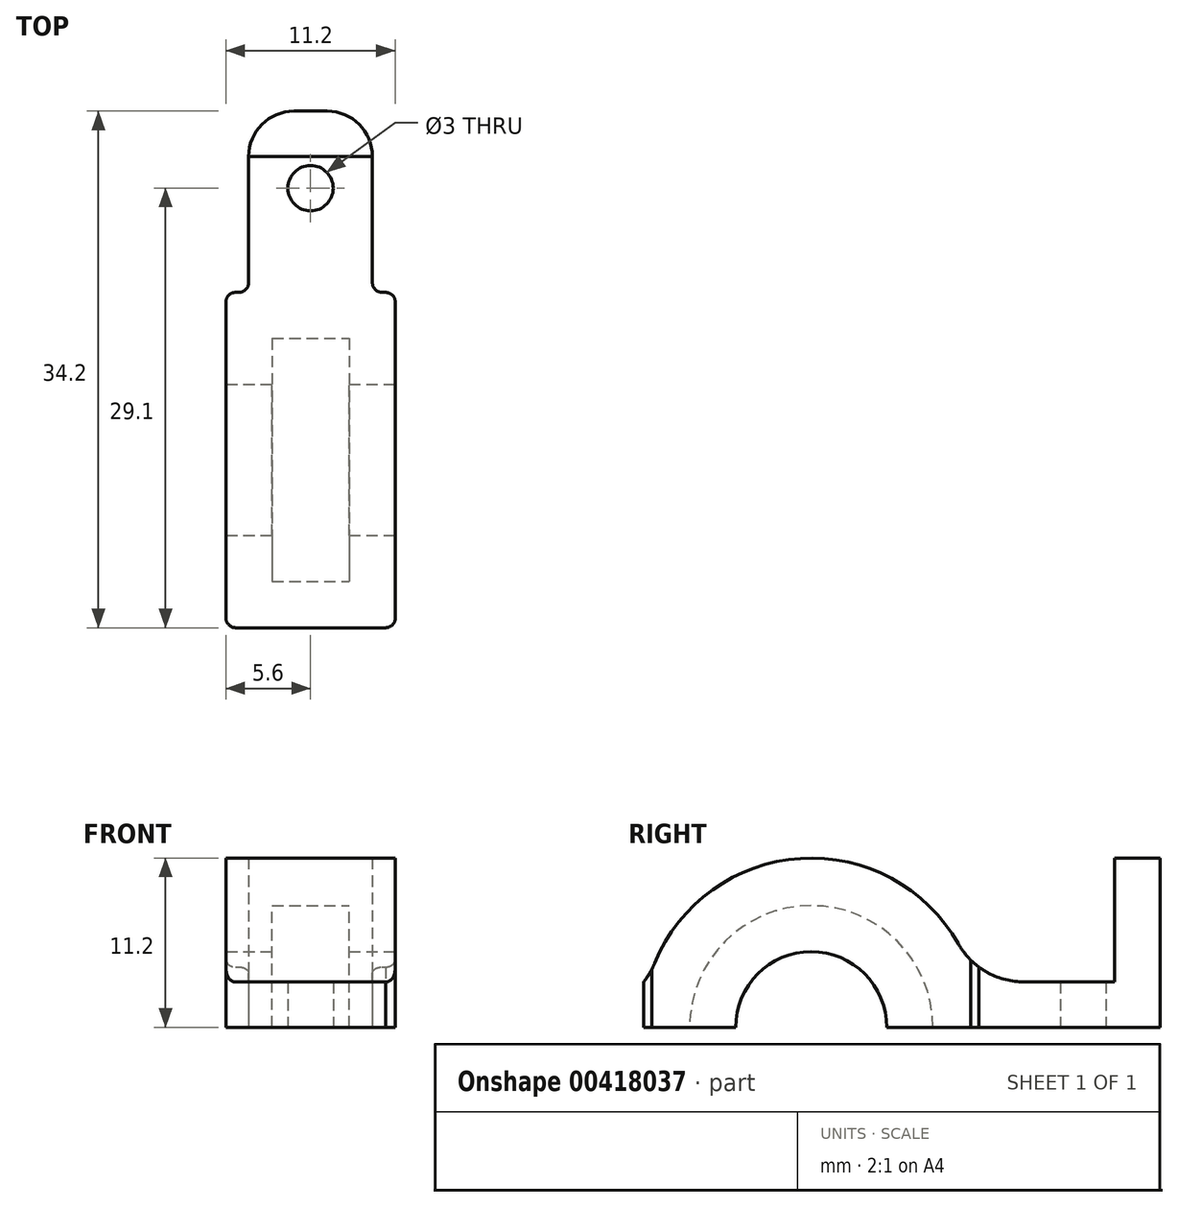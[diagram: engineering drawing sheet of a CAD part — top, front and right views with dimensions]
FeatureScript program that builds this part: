
annotation { "Feature Type Name" : "Feature", "Feature Type Description" : "" }
export const myFeature = defineFeature(function(context is Context, id is Id, definition is map)
    precondition{}
    {
        {
            var Q0;
            Q0=qCreatedBy(makeId("Top.planeOp"),FACE);
            var sketch = newSketch(context, id + "F0", { "sketchPlane" : qUnion([Q0])});
            skLineSegment(sketch, "E0", {"start": v(0, 0) * mm, "end": v(2.6, 0) * mm, "construction": true});
            skLineSegment(sketch, "E1", {"start": v(2.6, 0) * mm, "end": v(2.6, 8.1) * mm});
            skLineSegment(sketch, "E2", {"start": v(2.6, 8.1) * mm, "end": v(2.6, -8.1) * mm});
            skLineSegment(sketch, "E3.MirrorCS", {"start": v(-2.6, 8.1) * mm, "end": v(-2.6, -8.1) * mm});
            skLineSegment(sketch, "E4", {"start": v(2.6, 8.1) * mm, "end": v(-2.6, 8.1) * mm});
            skLineSegment(sketch, "E5", {"start": v(-2.6, -8.1) * mm, "end": v(2.6, -8.1) * mm});
            skLineSegment(sketch, "E6.0", {"start": v(4.97, 11.1) * mm, "end": v(4.73, 11.1) * mm});
            skLineSegment(sketch, "E6.1", {"start": v(5.6, 10.57) * mm, "end": v(5.6, -11.1) * mm});
            skLineSegment(sketch, "E6.3", {"start": v(-5.6, 10.47) * mm, "end": v(-5.6, -11.1) * mm});
            skCircle(sketch, "E7", {"center": v(0, 18) * mm, "radius": 1.5 * mm});
            skLineSegment(sketch, "E8", {"start": v(-4.1, 11.73) * mm, "end": v(-4.1, 20.1) * mm});
            skLineSegment(sketch, "E9.MirrorCS", {"start": v(4.1, 11.73) * mm, "end": v(4.1, 20.1) * mm});
            skLineSegment(sketch, "E10", {"start": v(-1.1, 23.1) * mm, "end": v(1.1, 23.1) * mm});
            skLineSegment(sketch, "E11.trimOffspring", {"start": v(-4.73, 11.1) * mm, "end": v(-4.97, 11.1) * mm});
            skPoint(sketch, "E12.visualSharp", {"position": v(-4.1, 11.1) * mm});
            skArc(sketch, "E12.filletArc", {"start": v(-4.73, 11.1) * mm, "mid": v(-4.29, 11.29) * mm, "end": v(-4.1, 11.73) * mm});
            skPoint(sketch, "E13.visualSharp", {"position": v(-5.6, 11.1) * mm});
            skArc(sketch, "E13.filletArc", {"start": v(-4.97, 11.1) * mm, "mid": v(-5.41, 10.91) * mm, "end": v(-5.6, 10.47) * mm});
            skPoint(sketch, "E14.visualSharp", {"position": v(-4.1, 23.1) * mm});
            skArc(sketch, "E14.filletArc", {"start": v(-1.1, 23.1) * mm, "mid": v(-3.22, 22.22) * mm, "end": v(-4.1, 20.1) * mm});
            skArc(sketch, "E15.MirrorCS", {"start": v(1.1, 23.1) * mm, "mid": v(3.22, 22.22) * mm, "end": v(4.1, 20.1) * mm});
            skArc(sketch, "E16.MirrorCS", {"start": v(4.97, 11.1) * mm, "mid": v(5.38, 10.95) * mm, "end": v(5.6, 10.57) * mm});
            skArc(sketch, "E17.MirrorCS", {"start": v(4.73, 11.1) * mm, "mid": v(4.29, 11.29) * mm, "end": v(4.1, 11.73) * mm});
            skPoint(sketch, "E18.orphan", {"position": v(4.1, 11.1) * mm});
            skPoint(sketch, "E19.orphan", {"position": v(4.1, 23.1) * mm});
            skLineSegment(sketch, "E20", {"start": v(-4.73, 11.1) * mm, "end": v(4.73, 11.1) * mm});
            skArc(sketch, "E21.MirrorCS", {"start": v(-4.73, -11.1) * mm, "mid": v(-4.29, -11.29) * mm, "end": v(-4.1, -11.73) * mm});
            skLineSegment(sketch, "E22.MirrorCS", {"start": v(-4.73, -11.1) * mm, "end": v(-4.97, -11.1) * mm});
            skArc(sketch, "E23.MirrorCS", {"start": v(-4.97, -11.1) * mm, "mid": v(-5.41, -10.91) * mm, "end": v(-5.6, -10.47) * mm});
            skArc(sketch, "E24.MirrorCS", {"start": v(4.73, -11.1) * mm, "mid": v(4.29, -11.29) * mm, "end": v(4.1, -11.73) * mm});
            skLineSegment(sketch, "E25.MirrorCS", {"start": v(4.97, -11.1) * mm, "end": v(4.73, -11.1) * mm});
            skArc(sketch, "E26.MirrorCS", {"start": v(4.97, -11.1) * mm, "mid": v(5.38, -10.95) * mm, "end": v(5.6, -10.57) * mm});
            skPoint(sketch, "E27.MirrorP", {"position": v(-4.1, -11.1) * mm});
            skPoint(sketch, "E28.MirrorP", {"position": v(-5.6, -11.1) * mm});
            skLineSegment(sketch, "E29.MirrorCS", {"start": v(-4.73, -11.1) * mm, "end": v(4.73, -11.1) * mm});
            skPoint(sketch, "E30.MirrorP", {"position": v(4.1, -23.1) * mm});
            skArc(sketch, "E31.MirrorCS", {"start": v(1.1, -23.1) * mm, "mid": v(3.22, -22.22) * mm, "end": v(4.1, -20.1) * mm});
            skCircle(sketch, "E32.MirrorC", {"center": v(0, -18) * mm, "radius": 1.5 * mm});
            skLineSegment(sketch, "E33.MirrorCS", {"start": v(-4.1, -11.73) * mm, "end": v(-4.1, -20.1) * mm});
            skPoint(sketch, "E34.MirrorP", {"position": v(-4.1, -23.1) * mm});
            skPoint(sketch, "E35.MirrorP", {"position": v(4.1, -11.1) * mm});
            skLineSegment(sketch, "E36.MirrorCS", {"start": v(4.1, -11.73) * mm, "end": v(4.1, -20.1) * mm});
            skLineSegment(sketch, "E37.MirrorCS", {"start": v(-1.1, -23.1) * mm, "end": v(1.1, -23.1) * mm});
            skArc(sketch, "E38.MirrorCS", {"start": v(-1.1, -23.1) * mm, "mid": v(-3.22, -22.22) * mm, "end": v(-4.1, -20.1) * mm});
            skLineSegment(sketch, "E39", {"start": v(0, 0) * mm, "end": v(5.6, 0) * mm});
            skLineSegment(sketch, "E40", {"start": v(0, 0) * mm, "end": v(-2.6, 0) * mm});
            skLineSegment(sketch, "E41.bottom", {"start": v(-2.55, -8.05) * mm, "end": v(2.55, -8.05) * mm});
            skLineSegment(sketch, "E41.top", {"start": v(-2.55, 8.05) * mm, "end": v(2.55, 8.05) * mm});
            skLineSegment(sketch, "E41.left", {"start": v(-2.55, -8.05) * mm, "end": v(-2.55, 8.05) * mm});
            skLineSegment(sketch, "E41.right", {"start": v(2.55, -8.05) * mm, "end": v(2.55, 8.05) * mm});
            skPoint(sketch, "E41.middle", {"position": v(0, 0) * mm});
            skSolve(sketch);
        }
        {
            var Q0;
            Q0=makeQuery(id+"F0.imprint","IMPRINT",FACE,{"disambiguationData":[TD([[makeQuery(id+"F0.imprint","IMPRINT",EDGE,{"derivedFrom":sQuery(id+"F0.wireOp",EDGE,"E7")}),-1.0]])]});
            var Q1;
            Q1=makeQuery(id+"F0.imprint","IMPRINT",FACE,{"disambiguationData":[TD([[makeQuery(id+"F0.imprint","IMPRINT",EDGE,{"derivedFrom":sQuery(id+"F0.wireOp",EDGE,"E3.MirrorCS")}),-1.0]])]});
            var Q2;
            {var subQ1=sQuery(id+"F0.wireOp",EDGE,"7e61b978-d09d-4bad-839f-0245cd0e4011.MirrorCS");Q2=makeQuery(id+"F0.imprint","IMPRINT",FACE,{"disambiguationData":[TD([[makeQuery(id+"F0.imprint","IMPRINT",EDGE,{"derivedFrom":subQ1}),1.0]])]});}
            var Q3;
            Q3=makeQuery(id+"F0.imprint","IMPRINT",FACE,{"disambiguationData":[TD([[makeQuery(id+"F0.imprint","IMPRINT",EDGE,{"derivedFrom":sQuery(id+"F0.wireOp",EDGE,"E3.MirrorCS")}),1.0]])]});
            var Q4;
            Q4=makeQuery(id+"F0.imprint","IMPRINT",FACE,{"disambiguationData":[TD([[makeQuery(id+"F0.imprint","IMPRINT",EDGE,{"derivedFrom":sQuery(id+"F0.wireOp",EDGE,"E21.MirrorCS")}),1.0]])]});
            var Q5;
            {var subQ1=sQuery(id+"F0.wireOp",EDGE,"E41.bottom");Q5=makeQuery(id+"F0.imprint","IMPRINT",FACE,{"disambiguationData":[TD([[makeQuery(id+"F0.imprint","IMPRINT",EDGE,{"derivedFrom":subQ1}),1.0]])]});}
            var Q6;
            {var subQ1=sQuery(id+"F0.wireOp",EDGE,"E41.top");Q6=makeQuery(id+"F0.imprint","IMPRINT",FACE,{"disambiguationData":[TD([[makeQuery(id+"F0.imprint","IMPRINT",EDGE,{"derivedFrom":subQ1}),-1.0]])]});}
            extrude(context, id + "F1", {"entities" : qUnion([Q0, Q1, Q2, Q3, Q4, Q5, Q6]), "depth" : (8.2 + 3) * mm});
        }
        {
            var Q0;
            Q0=makeQuery(id+"F1.opExtrude","SWEPT_FACE",FACE,{"disambiguationData":[OSD([sQuery(id+"F0.wireOp",EDGE,"E6.1")])]});
            var sketch = newSketch(context, id + "F2", { "sketchPlane" : qUnion([Q0])});
            skLineSegment(sketch, "E42.0.0", {"start": v(-23.1, 0) * mm, "end": v(-20.1, 0) * mm});
            skLineSegment(sketch, "E42.0.1", {"start": v(-20.1, 0) * mm, "end": v(-20.1, 11.2) * mm});
            skLineSegment(sketch, "E42.0.2", {"start": v(-20.1, 11.2) * mm, "end": v(-23.1, 11.2) * mm});
            skLineSegment(sketch, "E42.0.3", {"start": v(-23.1, 11.2) * mm, "end": v(-23.1, 0) * mm});
            skLineSegment(sketch, "E43.0.0", {"start": v(20.1, 0) * mm, "end": v(23.1, 0) * mm});
            skLineSegment(sketch, "E43.0.1", {"start": v(23.1, 0) * mm, "end": v(23.1, 11.2) * mm});
            skLineSegment(sketch, "E43.0.2", {"start": v(23.1, 11.2) * mm, "end": v(20.1, 11.2) * mm});
            skLineSegment(sketch, "E43.0.3", {"start": v(20.1, 11.2) * mm, "end": v(20.1, 0) * mm});
            skLineSegment(sketch, "E44.0.0", {"start": v(-10.57, 0) * mm, "end": v(10.57, 0) * mm});
            skLineSegment(sketch, "E44.0.1", {"start": v(10.57, 0) * mm, "end": v(10.57, 11.2) * mm});
            skLineSegment(sketch, "E44.0.2", {"start": v(10.57, 11.2) * mm, "end": v(-10.57, 11.2) * mm});
            skLineSegment(sketch, "E44.0.3", {"start": v(-10.57, 11.2) * mm, "end": v(-10.57, 0) * mm});
            skLineSegment(sketch, "E45.bottom", {"start": v(-23.1, 11.2) * mm, "end": v(23.1, 11.2) * mm});
            skLineSegment(sketch, "E45.top", {"start": v(-23.1, 3) * mm, "end": v(23.1, 3) * mm});
            skLineSegment(sketch, "E45.left", {"start": v(-23.1, 11.2) * mm, "end": v(-23.1, 3) * mm});
            skLineSegment(sketch, "E45.right", {"start": v(23.1, 11.2) * mm, "end": v(23.1, 3) * mm});
            skCircle(sketch, "E46", {"center": v(0, 0) * mm, "radius": 5 * mm});
            skCircle(sketch, "E47", {"center": v(0, 0) * mm, "radius": 11.2 * mm});
            skSolve(sketch);
        }
        {
            var Q0;
            {var subQ0=sQuery(id+"F2.wireOp",EDGE,"E45.bottom");var subQ3=sQuery(id+"F2.wireOp",EDGE,"E42.0.1");var subQ4=makeQuery(id+"F2.imprint","INTERSECT",VERTEX,{"derivedFrom":[subQ3,subQ0]});Q0=makeQuery(id+"F2.imprint","IMPRINT",FACE,{"disambiguationData":[TD([[makeQuery(id+"F2.imprint","IMPRINT",EDGE,{"disambiguationData":[TD([[subQ4,1.0]])],"derivedFrom":subQ3}),-1.0]])]});}
            var Q1;
            {var subQ5=sQuery(id+"F2.wireOp",EDGE,"E45.left");Q1=makeQuery(id+"F2.imprint","IMPRINT",FACE,{"disambiguationData":[TD([[makeQuery(id+"F2.imprint","IMPRINT",EDGE,{"derivedFrom":subQ5}),1.0]])]});}
            var Q2;
            {var subQ0=sQuery(id+"F2.wireOp",EDGE,"E45.bottom");var subQ1=sQuery(id+"F2.wireOp",EDGE,"E44.0.3");var subQ2=makeQuery(id+"F2.imprint","INTERSECT",VERTEX,{"derivedFrom":[subQ1,subQ0]});Q2=makeQuery(id+"F2.imprint","IMPRINT",FACE,{"disambiguationData":[TD([[makeQuery(id+"F2.imprint","IMPRINT",EDGE,{"disambiguationData":[TD([[subQ2,-1.0]])],"derivedFrom":subQ1}),1.0]])]});}
            var Q3;
            {var subQ0=sQuery(id+"F2.wireOp",EDGE,"E45.bottom");var subQ1=sQuery(id+"F2.wireOp",EDGE,"E44.0.1");var subQ2=makeQuery(id+"F2.imprint","INTERSECT",VERTEX,{"derivedFrom":[subQ1,subQ0]});Q3=makeQuery(id+"F2.imprint","IMPRINT",FACE,{"disambiguationData":[TD([[makeQuery(id+"F2.imprint","IMPRINT",EDGE,{"disambiguationData":[TD([[subQ2,-1.0]])],"derivedFrom":subQ1}),-1.0]])]});}
            var Q4;
            {var subQ1=sQuery(id+"F2.wireOp",EDGE,"E43.0.3");var subQ5=sQuery(id+"F2.wireOp",EDGE,"E45.bottom");var subQ8=makeQuery(id+"F2.imprint","INTERSECT",VERTEX,{"derivedFrom":[subQ1,subQ5]});Q4=makeQuery(id+"F2.imprint","IMPRINT",FACE,{"disambiguationData":[TD([[makeQuery(id+"F2.imprint","IMPRINT",EDGE,{"disambiguationData":[TD([[subQ8,-1.0]])],"derivedFrom":subQ1}),-1.0]])]});}
            var Q5;
            {var subQ5=sQuery(id+"F2.wireOp",EDGE,"E45.right");Q5=makeQuery(id+"F2.imprint","IMPRINT",FACE,{"disambiguationData":[TD([[makeQuery(id+"F2.imprint","IMPRINT",EDGE,{"derivedFrom":subQ5}),-1.0]])]});}
            var Q6;
            {var subQ0=sQuery(id+"F2.wireOp",EDGE,"E46");var subQ1=sQuery(id+"F2.wireOp",EDGE,"E44.0.0");var subQ2=makeQuery(id+"F2.imprint","INTERSECT",VERTEX,{"disambiguationData":[OD(0.0)],"derivedFrom":[subQ1,subQ0]});Q6=makeQuery(id+"F2.imprint","IMPRINT",FACE,{"disambiguationData":[TD([[makeQuery(id+"F2.imprint","IMPRINT",EDGE,{"disambiguationData":[TD([[subQ2,-1.0]])],"derivedFrom":subQ1}),-1.0]])]});}
            var Q7;
            {var subQ0=sQuery(id+"F2.wireOp",EDGE,"E46");var subQ1=sQuery(id+"F2.wireOp",EDGE,"E45.top");var subQ2=makeQuery(id+"F2.imprint","INTERSECT",VERTEX,{"disambiguationData":[OD(0.0)],"derivedFrom":[subQ1,subQ0]});Q7=makeQuery(id+"F2.imprint","IMPRINT",FACE,{"disambiguationData":[TD([[makeQuery(id+"F2.imprint","IMPRINT",EDGE,{"disambiguationData":[TD([[subQ2,-1.0]])],"derivedFrom":subQ1}),1.0]])]});}
            extrude(context, id + "F3", {"entities" : qUnion([Q0, Q1, Q2, Q3, Q4, Q5, Q6, Q7]), "operationType" : NewBodyOperationType.REMOVE, "oppositeDirection" : true, "depth" : 25 * mm});
        }
        {
            var Q0;
            {var subQ1=sQuery(id+"F0.wireOp",EDGE,"E41.bottom");Q0=makeQuery(id+"F0.imprint","IMPRINT",FACE,{"disambiguationData":[TD([[makeQuery(id+"F0.imprint","IMPRINT",EDGE,{"derivedFrom":subQ1}),1.0]])]});}
            var Q1;
            Q1=sQuery(id+"F0.wireOp",EDGE,"E39");
            revolve(context, id + "F4", {"operationType" : NewBodyOperationType.REMOVE, "entities" : qUnion([Q0]), "axis" : qUnion([Q1]), "revolveType" : RevolveType.FULL, "oppositeDirection" : true});
        }
        {
            var Q0;
            {var subQ0=sQuery(id+"F2.wireOp",EDGE,"E47");var subQ1=sQuery(id+"F2.wireOp",EDGE,"E45.top");Q0=makeQuery(id+"F3.boolean.opBoolean","COPY",EDGE,{"derivedFrom":makeQuery(id+"F3.opExtrude","SWEPT_EDGE",EDGE,{"disambiguationData":[OSD([subQ1,subQ0]),TDD([makeQuery(id+"F2.imprint","INTERSECT",VERTEX,{"disambiguationData":[OD(0.0)],"derivedFrom":[subQ1,subQ0]})])]})});}
            var Q1;
            {var subQ0=sQuery(id+"F2.wireOp",EDGE,"E47");var subQ1=sQuery(id+"F2.wireOp",EDGE,"E45.top");Q1=makeQuery(id+"F3.boolean.opBoolean","COPY",EDGE,{"derivedFrom":makeQuery(id+"F3.opExtrude","SWEPT_EDGE",EDGE,{"disambiguationData":[OSD([subQ1,subQ0]),TDD([makeQuery(id+"F2.imprint","INTERSECT",VERTEX,{"disambiguationData":[OD(1.0)],"derivedFrom":[subQ1,subQ0]})])]})});}
            fillet(context, id + "F5", {"entities" : qUnion([Q0, Q1]), "radius" : 5 * mm, "tangentPropagation" : true, "allowEdgeOverflow" : false});
        }
    });
